# Revit family: Lighting-Luminii-Leto_11_Mini_MP new
name_source: partatom
category: Lighting Fixtures
units: mm (PartAtom-declared; Revit-internal decimal feet)

## family parameters
Cut with Voids When Loaded = No
Host = Face
Light Source = Yes
OmniClass Number = 23.80.70.11.14.21
OmniClass Title = Spots and Tracklight Specialties
Part Type = Normal
Room Calculation Point = No
Round Connector Dimension = Use Diameter
Shared = Yes

## types (1)
- Not A Type - Load Type Catalog
    Apparent Load = 6 VA
    Assembly Code = D5040.50
    C Canopy Constraint = 3
    C Canopy Diameter = 0' - 3 1/2"
    C Canopy Height = 0' - 0 1/8"
    C Round Canopy = Yes
    C Square Canopy = No
    C Stem Height = 0' - 1"
    Color Filter = 16777215
    Current Amps = 0 A
    Default Elevation = 0' - 0"
    Description = Small Adjustable Spotlight
    Dimming Lamp Color Temperature Shift = <None>
    Driver = Standard - Non-Dimming
    Driver Comment = Contact Manufacture for Additional Driver Options
    Environment = Damp
    Frequency = 0 Hz
    Height = 0' - 3 179/256"
    Housing Protection Rating = IP20 Dry/IP66 Wet Series
    Initial Color Comments = Perfomance based on 3000K Photometric Web File
    Instruction Sheet Link = https://www.luminii.com
    Keynote = 26 51 00
    Lamp = LED
    Lens Material = Plastic - Luminii - Frosted Lens
    Load Classification = Lighting
    Lumen Output = 700
    Manufacturer = Luminii
    Model = Please Load Accompanying Type Catalog (.txt)
    Mounting Method = Track
    Number of Poles = 1
    Optic = 17"
    Phase = 1
    Photometric Web File = Leto 11 Mini T - 662-A90-617-35-15-00.ies
    Power Factor = 1
    Power Source Type = Driver
    Product Documentation Link = https://www.luminii.com
    Product Name = Leto 11 Mini MP
    Product Page URL = https://www.luminii.com
    Tilt Angle = -90.00°
    URL = https://www.luminii.com
    Version = 2020 - v1.0a
    Voltage = 120 V
    Voltage Comments = 120V
    Warranty URL = https://www.luminii.com
    Wattage Comments = 6.1 Watts
    Width = 0' - 2 1/2"

## geometry (parser evidence)
native form markers: Sweep x7
no freeform markers — native parametric forms only
